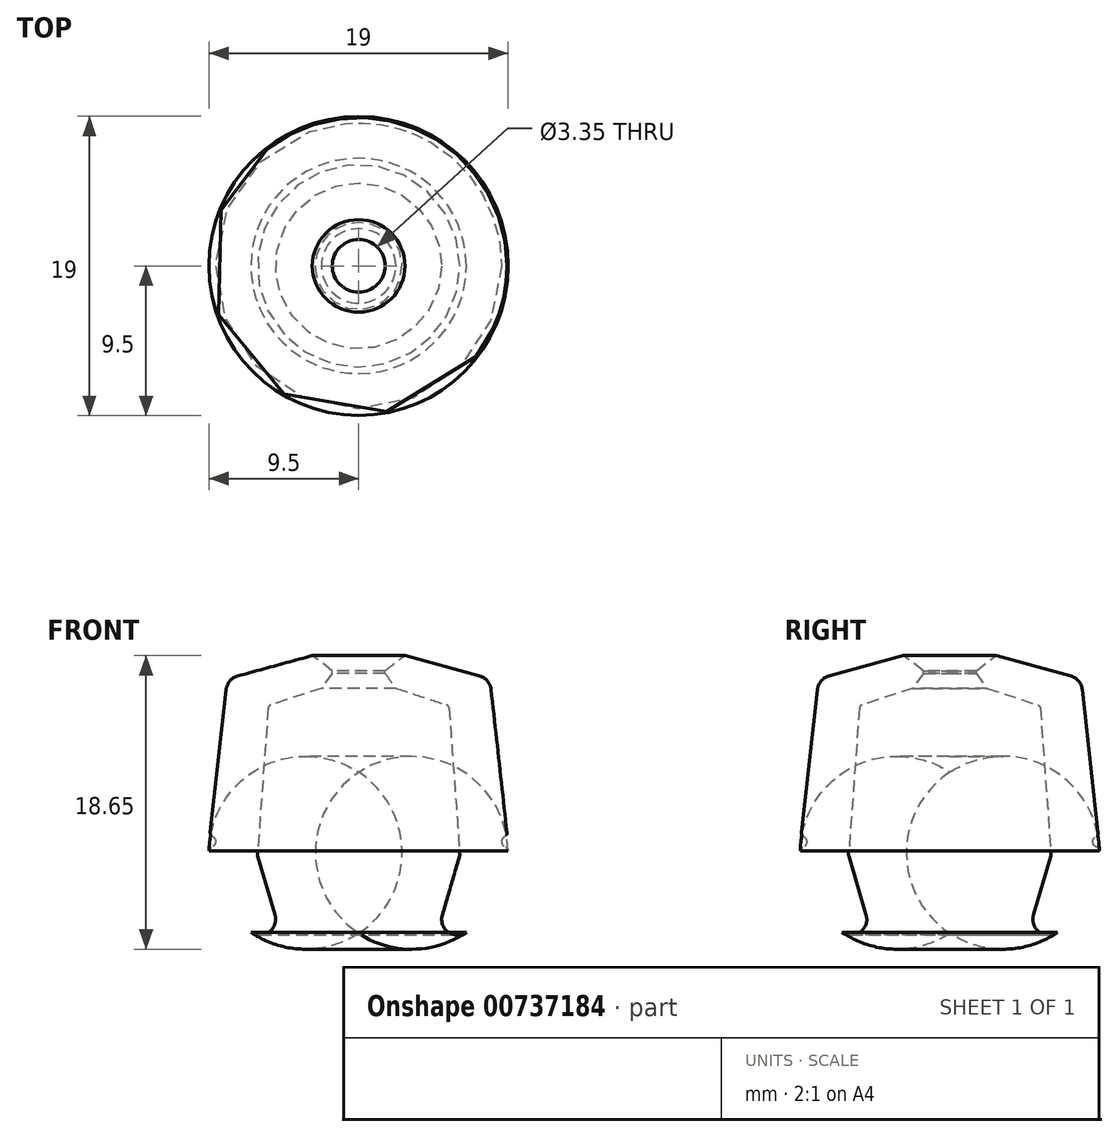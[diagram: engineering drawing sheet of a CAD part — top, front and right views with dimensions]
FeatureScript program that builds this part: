
annotation { "Feature Type Name" : "Feature", "Feature Type Description" : "" }
export const myFeature = defineFeature(function(context is Context, id is Id, definition is map)
    precondition{}
    {
        {
            var Q0;
            Q0=qCreatedBy(makeId("Front.planeOp"),FACE);
            var sketch = newSketch(context, id + "F0", { "sketchPlane" : qUnion([Q0])});
            skPoint(sketch, "E0.middle", {"position": v(0, 0) * mm});
            skLineSegment(sketch, "E1.right", {"start": v(1.68, 9.8) * mm, "end": v(1.68, 7.61) * mm});
            skPoint(sketch, "E2.orphan", {"position": v(9, -9) * mm});
            skPoint(sketch, "E0.right.end.orphan", {"position": v(-9, -9) * mm});
            skPoint(sketch, "E3.orphan", {"position": v(-9, 9) * mm});
            skPoint(sketch, "E4.orphan", {"position": v(9, 9) * mm});
            skPoint(sketch, "E1.bottom.start.orphan", {"position": v(0, 9) * mm});
            skLineSegment(sketch, "E5", {"start": v(0, 7.5) * mm, "end": v(0, 4.5) * mm});
            skPoint(sketch, "E6.start.orphan", {"position": v(2.81, -6.5) * mm});
            skPoint(sketch, "E7.start.orphan", {"position": v(8.27, 7.18) * mm});
            skPoint(sketch, "E8.start.orphan", {"position": v(9.07, 7.18) * mm});
            skArc(sketch, "E9", {"start": v(4.72, -9.04) * mm, "mid": v(8.26, -6.76) * mm, "end": v(9.5, -2.74) * mm});
            skLineSegment(sketch, "E10", {"start": v(0, 12.9) * mm, "end": v(9.5, 12.9) * mm});
            skPoint(sketch, "E11.orphan", {"position": v(3.25, -9.2) * mm});
            skPoint(sketch, "E1.left.end.orphan", {"position": v(0, -6.5) * mm});
            skPoint(sketch, "E12.center.orphan", {"position": v(0, -8.43) * mm});
            skPoint(sketch, "E13.start.orphan", {"position": v(9.5, -0.9) * mm});
            skArc(sketch, "E14", {"start": v(9.44, -2) * mm, "mid": v(9.09, -2.39) * mm, "end": v(9.5, -2.74) * mm});
            skLineSegment(sketch, "E15", {"start": v(1.68, 9.8) * mm, "end": v(8.34, 7.98) * mm});
            skLineSegment(sketch, "E16", {"start": v(8.34, 7.98) * mm, "end": v(9.44, -2) * mm});
            skPoint(sketch, "E17.start.orphan", {"position": v(2, -2.03) * mm});
            skPoint(sketch, "E18.center.orphan", {"position": v(0, 1.16) * mm});
            skPoint(sketch, "E19.visualSharp", {"position": v(4.72, 5.47) * mm});
            skArc(sketch, "E19.filletArc", {"start": v(4.72, 5.38) * mm, "mid": v(4.7, 5.46) * mm, "end": v(4.66, 5.54) * mm});
            skLineSegment(sketch, "E20", {"start": v(1.68, 7.61) * mm, "end": v(5.6, 6.32) * mm});
            skLineSegment(sketch, "E21", {"start": v(5.75, 6.13) * mm, "end": v(6.43, -3.17) * mm});
            skLineSegment(sketch, "E22", {"start": v(6.42, -3.25) * mm, "end": v(4.72, -9.04) * mm});
            skPoint(sketch, "E23.visualSharp", {"position": v(5.73, 6.27) * mm});
            skArc(sketch, "E23.filletArc", {"start": v(5.75, 6.13) * mm, "mid": v(5.7, 6.25) * mm, "end": v(5.6, 6.32) * mm});
            skPoint(sketch, "E24.visualSharp", {"position": v(6.43, -3.21) * mm});
            skArc(sketch, "E24.filletArc", {"start": v(6.42, -3.25) * mm, "mid": v(6.43, -3.21) * mm, "end": v(6.43, -3.17) * mm});
            skSolve(sketch);
        }
        {
            var Q0;
            Q0=makeQuery(id+"F0.imprint","IMPRINT",FACE,{"disambiguationData":[TD([[makeQuery(id+"F0.imprint","IMPRINT",EDGE,{"derivedFrom":sQuery(id+"F0.wireOp",EDGE,"E1.right")}),1.0]])]});
            var Q1;
            Q1=sQuery(id+"F0.wireOp",EDGE,"E5");
            revolve(context, id + "F1", {"surfaceOperationType" : NewSurfaceOperationType.NEW, "entities" : qUnion([Q0]), "axis" : qUnion([Q1]), "revolveType" : RevolveType.FULL});
        }
        {
            var Q0;
            Q0=makeQuery(id+"F1.opRevolve","SWEPT_EDGE",EDGE,{"disambiguationData":[OSD([sQuery(id+"F0.wireOp",EDGE,"0hkBze6B-r9Oy-IiPh-F7lh-CEgiL7ndkA8u"),sQuery(id+"F0.wireOp",EDGE,"E14")])]});
            var Q1;
            Q1=makeQuery(id+"F1.opRevolve","SWEPT_EDGE",EDGE,{"disambiguationData":[OSD([sQuery(id+"F0.wireOp",EDGE,"E9"),sQuery(id+"F0.wireOp",EDGE,"E14")])]});
            fillet(context, id + "F2", {"entities" : qUnion([Q0, Q1]), "radius" : .25 * mm, "tangentPropagation" : true, "allowEdgeOverflow" : false});
        }
        {
            var Q0;
            Q0=makeQuery(id+"F1.opRevolve","SWEPT_EDGE",EDGE,{"disambiguationData":[OSD([sQuery(id+"F0.wireOp",EDGE,"E1.right"),sQuery(id+"F0.wireOp",EDGE,"W14FOtLs-EhAw-IuQ9-SR6E-mXUHSF7JRKLb")])]});
            chamfer(context, id + "F3", {"entities" : qUnion([Q0]), "width" : 1 * mm, "tangentPropagation" : true});
        }
        {
            var Q0;
            Q0=makeQuery(id+"F1.opRevolve","SWEPT_EDGE",EDGE,{"disambiguationData":[OSD([sQuery(id+"F0.wireOp",EDGE,"IHR5pVOM-uiN5-Okhq-o9gd-xioHJXAe0way"),sQuery(id+"F0.wireOp",EDGE,"E9")])]});
            fillet(context, id + "F4", {"entities" : qUnion([Q0]), "radius" : 1 * mm, "tangentPropagation" : true, "defaultsChanged" : true, "vertexSettings" : [], "allowEdgeOverflow" : false});
        }
        {
            var Q0;
            Q0=makeQuery(id+"F1.opRevolve","SWEPT_EDGE",EDGE,{"disambiguationData":[OSD([sQuery(id+"F0.wireOp",EDGE,"E15"),sQuery(id+"F0.wireOp",EDGE,"E16")])]});
            fillet(context, id + "F5", {"entities" : qUnion([Q0]), "tangentPropagation" : true, "radius" : 1 * mm, "defaultsChanged" : true, "vertexSettings" : [], "allowEdgeOverflow" : false});
        }
    });
